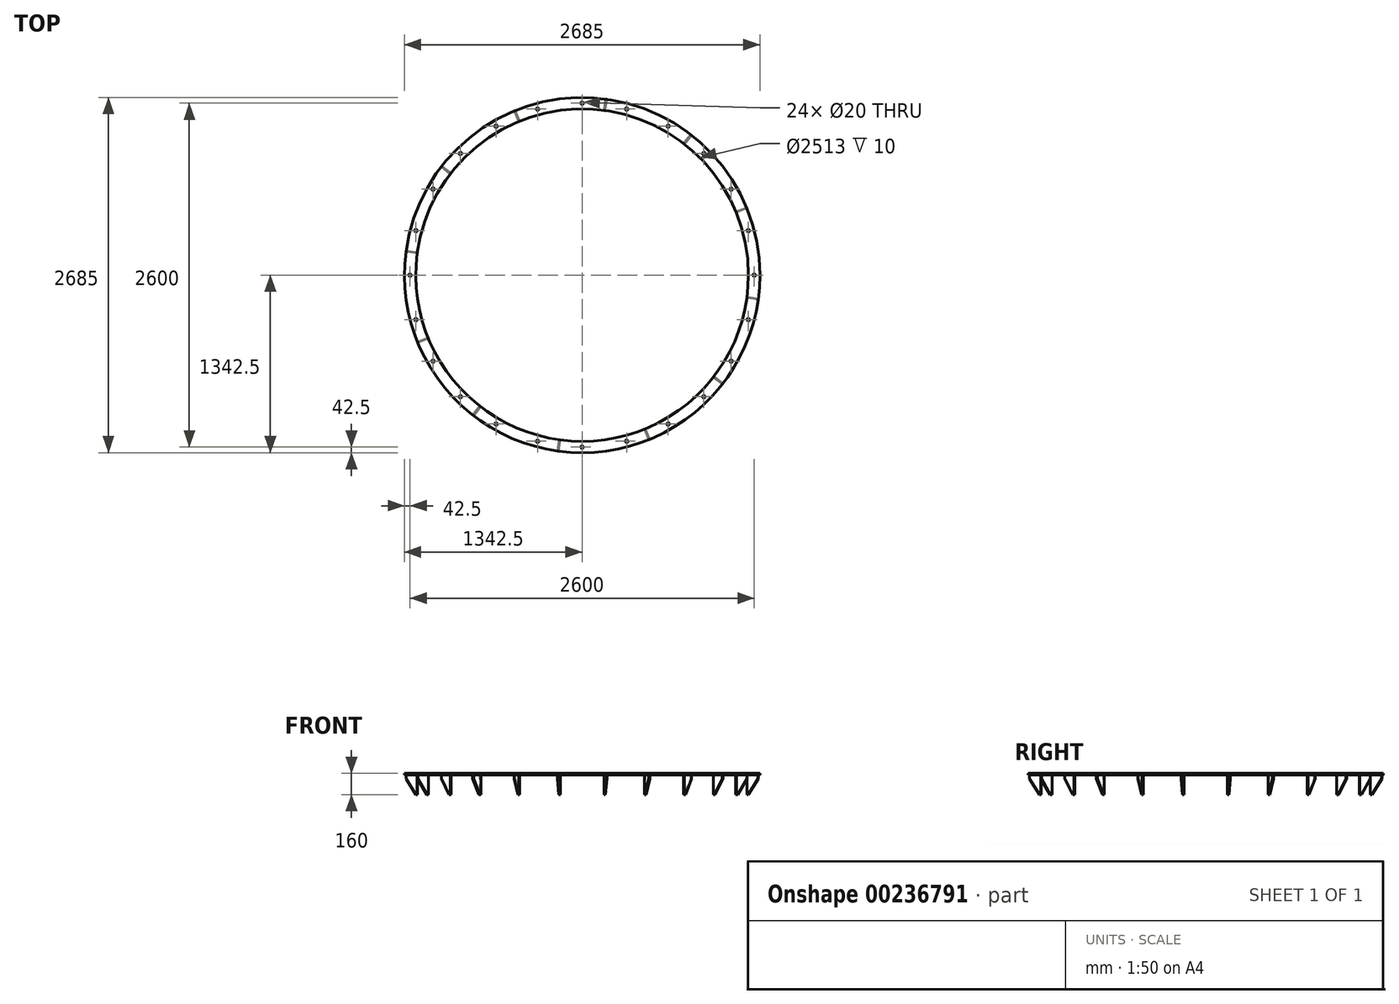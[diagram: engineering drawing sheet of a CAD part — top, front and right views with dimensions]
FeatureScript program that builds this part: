
annotation { "Feature Type Name" : "Feature", "Feature Type Description" : "" }
export const myFeature = defineFeature(function(context is Context, id is Id, definition is map)
    precondition{}
    {
        {
            var Q0;
            Q0=qCreatedBy(makeId("Top.planeOp"),FACE);
            var sketch = newSketch(context, id + "F0", { "sketchPlane" : qUnion([Q0])});
            skCircle(sketch, "E0", {"center": v(0, 0) * mm, "radius": 1342.5 * mm});
            skCircle(sketch, "E1", {"center": v(0, 0) * mm, "radius": 1256.5 * mm});
            skSolve(sketch);
        }
        {
            var Q0;
            Q0=makeQuery(id+"F0.imprint","IMPRINT",FACE,{"disambiguationData":[TD([[makeQuery(id+"F0.imprint","IMPRINT",EDGE,{"derivedFrom":sQuery(id+"F0.wireOp",EDGE,"E0")}),1.0]])]});
            extrude(context, id + "F1", {"entities" : qUnion([Q0]), "depth" : 10 * mm, "offsetDistance" : 25 * mm});
        }
        {
            var Q0;
            Q0=makeQuery(id+"F1.opExtrude","CAP_FACE",FACE,{"disambiguationData":[OSD([sQuery(id+"F0.wireOp",EDGE,"E0"),sQuery(id+"F0.wireOp",EDGE,"E1")])],"isStart":false});
            var sketch = newSketch(context, id + "F2", { "sketchPlane" : qUnion([Q0])});
            skPoint(sketch, "E2", {"position": v(0, 1300) * mm});
            skPoint(sketch, "E3.1.0", {"position": v(-336.46, 1255.7) * mm});
            skPoint(sketch, "E3.2.0", {"position": v(-650, 1125.83) * mm});
            skPoint(sketch, "E3.3.0", {"position": v(-919.24, 919.24) * mm});
            skPoint(sketch, "E3.4.0", {"position": v(-1125.83, 650) * mm});
            skPoint(sketch, "E3.5.0", {"position": v(-1255.7, 336.46) * mm});
            skPoint(sketch, "E3.6.0", {"position": v(-1300, 0) * mm});
            skPoint(sketch, "E3.7.0", {"position": v(-1255.7, -336.46) * mm});
            skPoint(sketch, "E3.8.0", {"position": v(-1125.83, -650) * mm});
            skPoint(sketch, "E3.9.0", {"position": v(-919.24, -919.24) * mm});
            skPoint(sketch, "E3.10.0", {"position": v(-650, -1125.83) * mm});
            skPoint(sketch, "E3.11.0", {"position": v(-336.46, -1255.7) * mm});
            skPoint(sketch, "E3.12.0", {"position": v(0, -1300) * mm});
            skPoint(sketch, "E3.13.0", {"position": v(336.46, -1255.7) * mm});
            skPoint(sketch, "E3.14.0", {"position": v(650, -1125.83) * mm});
            skPoint(sketch, "E3.15.0", {"position": v(919.24, -919.24) * mm});
            skPoint(sketch, "E3.16.0", {"position": v(1125.83, -650) * mm});
            skPoint(sketch, "E3.17.0", {"position": v(1255.7, -336.46) * mm});
            skPoint(sketch, "E3.18.0", {"position": v(1300, 0) * mm});
            skPoint(sketch, "E3.19.0", {"position": v(1255.7, 336.46) * mm});
            skPoint(sketch, "E3.20.0", {"position": v(1125.83, 650) * mm});
            skPoint(sketch, "E3.21.0", {"position": v(919.24, 919.24) * mm});
            skPoint(sketch, "E3.22.0", {"position": v(650, 1125.83) * mm});
            skPoint(sketch, "E3.23.0", {"position": v(336.46, 1255.7) * mm});
            skPoint(sketch, "E3.center", {"position": v(0, 0) * mm});
            skSolve(sketch);
        }
        {
            var Q0;
            Q0=sQuery(id+"F2.wireOp",VERTEX,"E2");
            var Q1;
            Q1=sQuery(id+"F2.wireOp",VERTEX,"E3.1.0");
            var Q2;
            Q2=sQuery(id+"F2.wireOp",VERTEX,"E3.2.0");
            var Q3;
            Q3=sQuery(id+"F2.wireOp",VERTEX,"E3.3.0");
            var Q4;
            Q4=sQuery(id+"F2.wireOp",VERTEX,"E3.4.0");
            var Q5;
            Q5=sQuery(id+"F2.wireOp",VERTEX,"E3.23.0");
            var Q6;
            Q6=sQuery(id+"F2.wireOp",VERTEX,"E3.22.0");
            var Q7;
            Q7=sQuery(id+"F2.wireOp",VERTEX,"E3.21.0");
            var Q8;
            Q8=sQuery(id+"F2.wireOp",VERTEX,"E3.20.0");
            var Q9;
            Q9=sQuery(id+"F2.wireOp",VERTEX,"E3.19.0");
            var Q10;
            Q10=sQuery(id+"F2.wireOp",VERTEX,"E3.18.0");
            var Q11;
            Q11=sQuery(id+"F2.wireOp",VERTEX,"E3.17.0");
            var Q12;
            Q12=sQuery(id+"F2.wireOp",VERTEX,"E3.16.0");
            var Q13;
            Q13=sQuery(id+"F2.wireOp",VERTEX,"E3.15.0");
            var Q14;
            Q14=sQuery(id+"F2.wireOp",VERTEX,"E3.14.0");
            var Q15;
            Q15=sQuery(id+"F2.wireOp",VERTEX,"E3.13.0");
            var Q16;
            Q16=sQuery(id+"F2.wireOp",VERTEX,"E3.12.0");
            var Q17;
            Q17=sQuery(id+"F2.wireOp",VERTEX,"E3.11.0");
            var Q18;
            Q18=sQuery(id+"F2.wireOp",VERTEX,"E3.10.0");
            var Q19;
            Q19=sQuery(id+"F2.wireOp",VERTEX,"E3.9.0");
            var Q20;
            Q20=sQuery(id+"F2.wireOp",VERTEX,"E3.8.0");
            var Q21;
            Q21=sQuery(id+"F2.wireOp",VERTEX,"E3.7.0");
            var Q22;
            Q22=sQuery(id+"F2.wireOp",VERTEX,"E3.6.0");
            var Q23;
            Q23=sQuery(id+"F2.wireOp",VERTEX,"E3.5.0");
            var Q24;
            Q24=makeQuery(id+"F1.opExtrude","SWEPT_BODY",BODY,{"disambiguationData":[OSD([sQuery(id+"F0.wireOp",EDGE,"E0"),sQuery(id+"F0.wireOp",EDGE,"E1")])]});
            hole(context, id + "F3", {"style" : HoleStyle.SIMPLE, "endStyle" : HoleEndStyle.THROUGH, "standardTappedOrClearance" : lookupTablePath({ "fit" : "Normal", "standard" : "ISO", "size" : "M18", "type" : "Clearance" }), "standardBlindInLast" : lookupTablePath({ "fit" : "Normal", "standard" : "ISO", "engagement" : "75%", "pitch" : "1.5 mm", "size" : "M18", "type" : "Clearance & tapped" }), "holeDiameter" : 20 * mm, "majorDiameter" : 5 * mm, "isTappedThrough" : true, "tappedDepth" : 28 * mm, "tapClearance" : 3, "locations" : qUnion([Q0, Q1, Q2, Q3, Q4, Q5, Q6, Q7, Q8, Q9, Q10, Q11, Q12, Q13, Q14, Q15, Q16, Q17, Q18, Q19, Q20, Q21, Q22, Q23]), "scope" : qUnion([Q24])});
        }
        {
            var Q0;
            Q0=makeQuery(id+"F1.opExtrude","CAP_FACE",FACE,{"disambiguationData":[OSD([sQuery(id+"F0.wireOp",EDGE,"E0"),sQuery(id+"F0.wireOp",EDGE,"E1")])],"isStart":true});
            var sketch = newSketch(context, id + "F4", { "sketchPlane" : qUnion([Q0])});
            skLineSegment(sketch, "E4", {"start": v(186.84, -1329.43) * mm, "end": v(174.87, -1244.23) * mm});
            skLineSegment(sketch, "E5", {"start": v(0, -1300) * mm, "end": v(0, 0) * mm});
            skLineSegment(sketch, "E6", {"start": v(186.84, -1329.43) * mm, "end": v(176.94, -1330.83) * mm});
            skLineSegment(sketch, "E7", {"start": v(176.94, -1330.83) * mm, "end": v(164.96, -1245.62) * mm});
            skLineSegment(sketch, "E8", {"start": v(164.96, -1245.62) * mm, "end": v(174.87, -1244.23) * mm});
            skSolve(sketch);
        }
        {
            var Q0;
            Q0 = qSketchRegion(id + "F4", true);
            extrude(context, id + "F5", {"entities" : qUnion([Q0]), "depth" : 150 * mm, "offsetDistance" : 25 * mm});
        }
        {
            var Q0;
            Q0=makeQuery(id+"F5.opExtrude","CAP_EDGE",EDGE,{"disambiguationData":[OSD([sQuery(id+"F4.wireOp",EDGE,"E6")])],"isStart":false});
            chamfer(context, id + "F6", {"entities" : qUnion([Q0]), "chamferType" : ChamferType.OFFSET_ANGLE, "width" : 120 * mm, "oppositeDirection" : false, "angle" : 32 * degree, "tangentPropagation" : true});
        }
        {
            var Q0;
            Q0=makeQuery(id+"F5.opExtrude","SWEPT_BODY",BODY,{"disambiguationData":[OSD([sQuery(id+"F4.wireOp",EDGE,"E4"),sQuery(id+"F4.wireOp",EDGE,"E6"),sQuery(id+"F4.wireOp",EDGE,"E7"),sQuery(id+"F4.wireOp",EDGE,"E8")])]});
            var Q1;
            Q1=makeQuery(id+"F1.opExtrude","CAP_EDGE",EDGE,{"disambiguationData":[OSD([sQuery(id+"F0.wireOp",EDGE,"E1")])],"isStart":false});
            circularPattern(context, id + "F7", {"operationType" : NewBodyOperationType.ADD, "entities" : qUnion([Q0]), "axis" : qUnion([Q1]), "angle" : 360 * degree, "instanceCount" : 12, "equalSpace" : true, "isCentered" : true});
        }
    });
